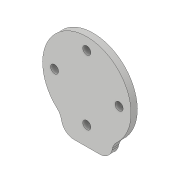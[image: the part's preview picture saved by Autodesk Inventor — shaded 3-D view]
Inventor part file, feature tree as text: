
AUTODESK INVENTOR PART (.ipt)
format: ipt  version: 2017 (Build 210142000, 142)  size: 272,896 bytes
history: native  units: in
note: dims shown in document units (in); Inventor stores cm internally (conversion verified against a paired STEP export)
features: sketch x8, extrude x5, projected_geometry x5, fillet x3, chamfer x2, sheet_metal_op x1, hole x1, other x1
ambient origin geometry x8: Origin, YZ Plane, XZ Plane, XY Plane, X Axis, Y Axis, Z Axis, Center Point
bodies: Solid1 (feature_tree)
feature tree (26):
  sheet_metal_op  "Face1"
  extrude  "Extrusion1"  Depth=0.3937in
  sketch  "Sketch3"  dims[d10=0.25in d11=0.25in]
  fillet  "Fillet4"  Radius=0.5512in
  extrude  "Extrusion2"  Depth=0.0623in
  extrude  "Extrusion3"  Depth=0.25in
  extrude  "Extrusion4"  Depth=0.125in
  fillet  "Fillet5"  Radius=1.0in
  chamfer  "Chamfer3"  Distance=0.2004in
  chamfer  "Chamfer4"  Distance=0.1in
  hole  "Hole1"  [1 undecoded]
  extrude  "Extrusion5"  TaperAngle=0.0deg  [1 undecoded]
  fillet  "Fillet6"  Radius=0.0179in
  sketch  "Sketch1"  dims[d2=0.1969in d3=0.3937in d4=0.5512in]
  other  "Plate1"
  sketch  "Sketch2"  dims[d8=0.0623in d9=0.0623in]
  projected_geometry  "Projected Loop1"
  sketch  "Sketch4"  dims[d12=0.062in d14=0.125in d15=1.0in d16=0.0in]
  projected_geometry  "Projected Loop2"
  sketch  "Sketch5"  dims[d18=0.0573in]
  projected_geometry  "Projected Loop3"
  sketch  "Sketch6"  dims[d19=0.0573in]
  sketch  "Sketch7"  dims[d28=0.2362in]
  projected_geometry  "Projected Loop4"
  sketch  "Sketch8"  dims[d29=0.125in d30=0.2004in d31=0.1in d32=0.1in d33=0.0in d34=0.0179in d35=0.315in d36=0.0573in d37=0.015in d38=1.0in d39=0.0in d40=0.1969in d42=1.0in d43=0.0in d44=0.1752in d45=0.862in d46=0.5in d47=1.0in d48=0.0in d49=0.125in d50=0.125in d51=0.125in d52=0.0137in d53=0.125in d54=0.125in d55=0.0137in d56=0.6299in d57=0.0787in d58=0.75in d59=0.375in d60=0.25in d61=0.5635in d62=0.062in d63=0.8108in d64=1.0in d65=0.0in d66=0.125in]
  projected_geometry  "Projected Loop5"
note: 2 required parameter values undecoded (feature->parameter linkage not recoverable at this tier; creation-order binding heuristic only, values carry confidence <= 0.55)
